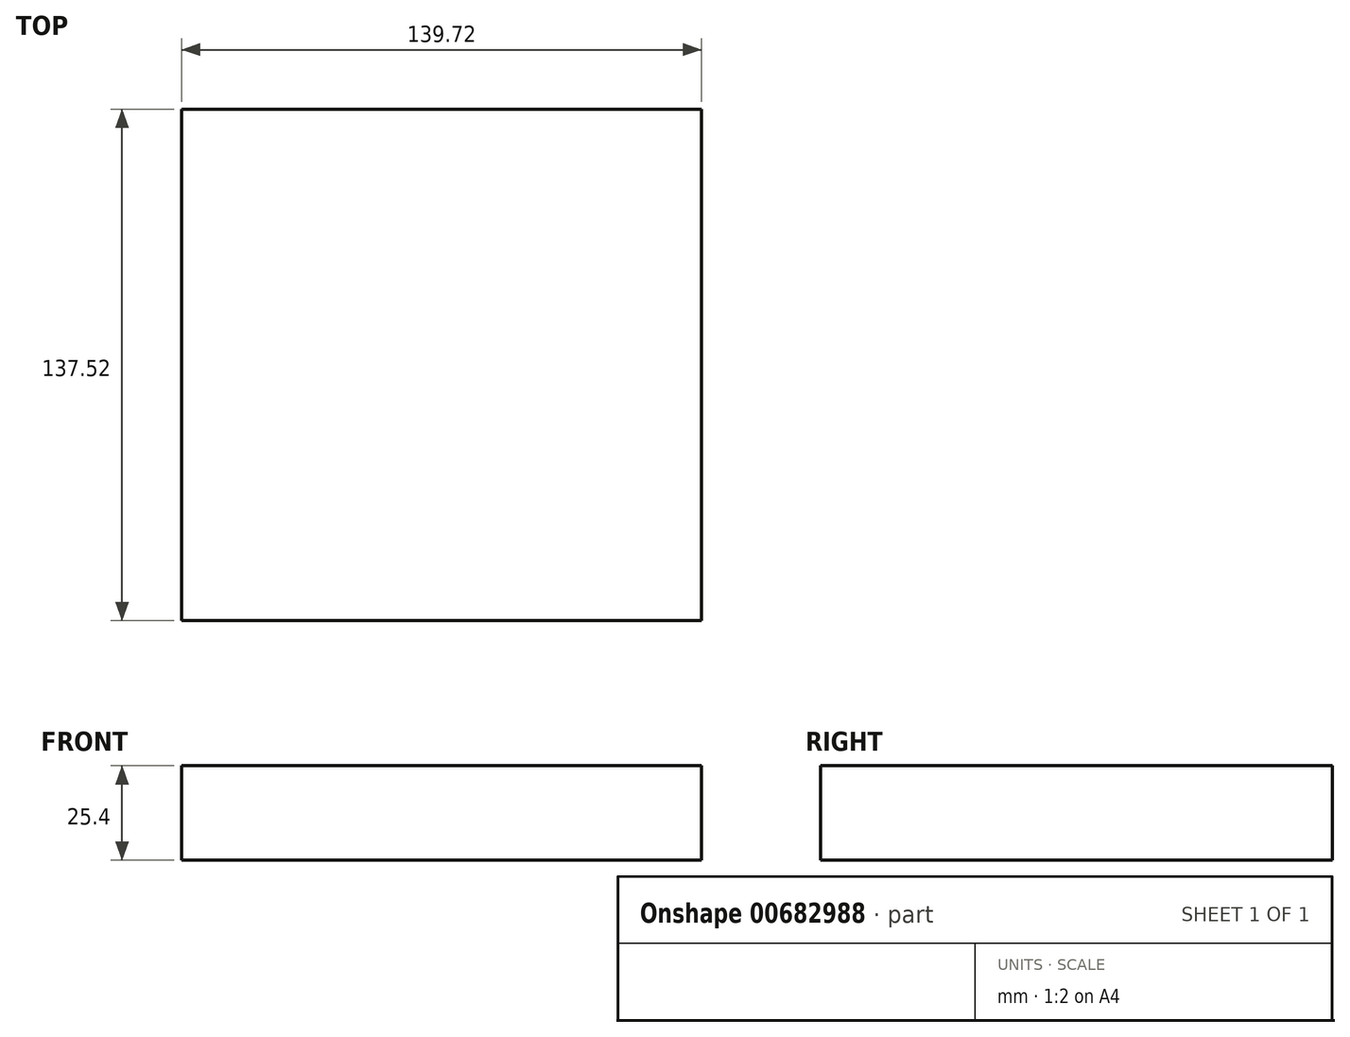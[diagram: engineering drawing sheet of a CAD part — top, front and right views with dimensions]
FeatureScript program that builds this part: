
annotation { "Feature Type Name" : "Feature", "Feature Type Description" : "" }
export const myFeature = defineFeature(function(context is Context, id is Id, definition is map)
    precondition{}
    {
        {
            var Q0;
            Q0=qCreatedBy(makeId("Top.planeOp"),FACE);
            var sketch = newSketch(context, id + "F0", { "sketchPlane" : qUnion([Q0])});
            skLineSegment(sketch, "E0.bottom", {"start": v(69.86, -68.76) * mm, "end": v(-69.86, -68.76) * mm});
            skLineSegment(sketch, "E0.top", {"start": v(69.86, 68.76) * mm, "end": v(-69.86, 68.76) * mm});
            skLineSegment(sketch, "E0.left", {"start": v(69.86, -68.76) * mm, "end": v(69.86, 68.76) * mm});
            skLineSegment(sketch, "E0.right", {"start": v(-69.86, -68.76) * mm, "end": v(-69.86, 68.76) * mm});
            skPoint(sketch, "E0.middle", {"position": v(0, 0) * mm});
            skLineSegment(sketch, "E1", {"start": v(0, 68.76) * mm, "end": v(0, -68.76) * mm});
            skSolve(sketch);
        }
        {
            var Q0;
            {var subQ0=sQuery(id+"F0.wireOp",EDGE,"E0.right");Q0=makeQuery(id+"F0.imprint","IMPRINT",FACE,{"disambiguationData":[TD([[makeQuery(id+"F0.imprint","IMPRINT",EDGE,{"derivedFrom":subQ0}),-1.0]])]});}
            extrude(context, id + "F1", {"entities" : qUnion([Q0]), "depth" : 25.4 * mm, "offsetDistance" : 25.4 * mm});
        }
        {
            var Q0;
            {var subQ0=sQuery(id+"F0.wireOp",EDGE,"E0.left");Q0=makeQuery(id+"F0.imprint","IMPRINT",FACE,{"disambiguationData":[TD([[makeQuery(id+"F0.imprint","IMPRINT",EDGE,{"derivedFrom":subQ0}),1.0]])]});}
            extrude(context, id + "F2", {"entities" : qUnion([Q0]), "operationType" : NewBodyOperationType.ADD, "depth" : 25.4 * mm, "offsetDistance" : 25.4 * mm});
        }
    });
